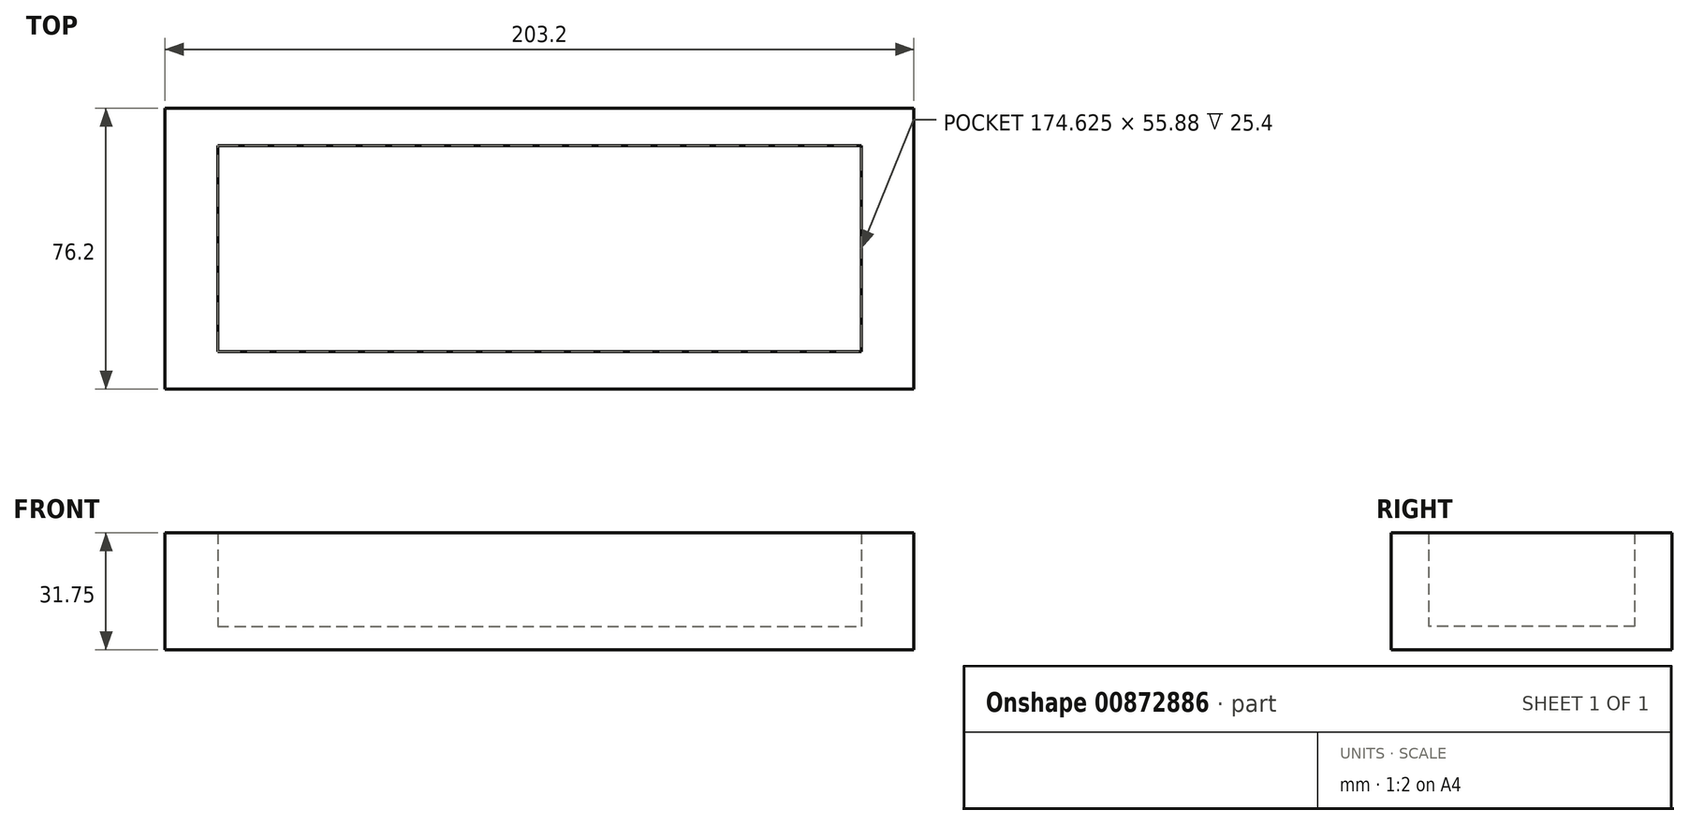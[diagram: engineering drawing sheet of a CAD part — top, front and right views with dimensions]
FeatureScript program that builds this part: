
annotation { "Feature Type Name" : "Feature", "Feature Type Description" : "" }
export const myFeature = defineFeature(function(context is Context, id is Id, definition is map)
    precondition{}
    {
        {
            var Q0;
            Q0=qCreatedBy(makeId("Top.planeOp"),FACE);
            var sketch = newSketch(context, id + "F0", { "sketchPlane" : qUnion([Q0])});
            skLineSegment(sketch, "E0.bottom", {"start": v(-101.6, 38.1) * mm, "end": v(101.6, 38.1) * mm});
            skLineSegment(sketch, "E0.top", {"start": v(-101.6, -38.1) * mm, "end": v(101.6, -38.1) * mm});
            skLineSegment(sketch, "E0.left", {"start": v(-101.6, 38.1) * mm, "end": v(-101.6, -38.1) * mm});
            skLineSegment(sketch, "E0.right", {"start": v(101.6, 38.1) * mm, "end": v(101.6, -38.1) * mm});
            skPoint(sketch, "E0.middle", {"position": v(0, 0) * mm});
            skSolve(sketch);
        }
        {
            var Q0;
            Q0=makeQuery(id+"F0.imprint","IMPRINT",FACE,{"disambiguationData":[TD([[makeQuery(id+"F0.imprint","IMPRINT",EDGE,{"derivedFrom":sQuery(id+"F0.wireOp",EDGE,"E0.bottom")}),-1.0]])]});
            var sketch = newSketch(context, id + "F1", { "sketchPlane" : qUnion([Q0])});
            skLineSegment(sketch, "E1.bottom", {"start": v(-87.31, 27.94) * mm, "end": v(87.31, 27.94) * mm});
            skLineSegment(sketch, "E1.top", {"start": v(-87.31, -27.94) * mm, "end": v(87.31, -27.94) * mm});
            skLineSegment(sketch, "E1.left", {"start": v(-87.31, 27.94) * mm, "end": v(-87.31, -27.94) * mm});
            skLineSegment(sketch, "E1.right", {"start": v(87.31, 27.94) * mm, "end": v(87.31, -27.94) * mm});
            skPoint(sketch, "E1.middle", {"position": v(0, 0) * mm});
            skSolve(sketch);
        }
        {
            var Q0;
            Q0=makeQuery(id+"F1.imprint","IMPRINT",FACE,{"disambiguationData":[TD([[makeQuery(id+"F1.imprint","IMPRINT",EDGE,{"derivedFrom":sQuery(id+"F1.wireOp",EDGE,"E1.bottom")}),1.0]])]});
            extrude(context, id + "F2", {"entities" : qUnion([Q0]), "depth" : 31.75 * mm, "offsetDistance" : 25.4 * mm});
        }
        {
            var Q0;
            Q0=makeQuery(id+"F0.imprint","IMPRINT",FACE,{"disambiguationData":[TD([[makeQuery(id+"F0.imprint","IMPRINT",EDGE,{"derivedFrom":sQuery(id+"F0.wireOp",EDGE,"E0.bottom")}),-1.0]])]});
            extrude(context, id + "F3", {"entities" : qUnion([Q0]), "operationType" : NewBodyOperationType.ADD, "depth" : 6.35 * mm, "offsetDistance" : 25.4 * mm});
        }
    });
